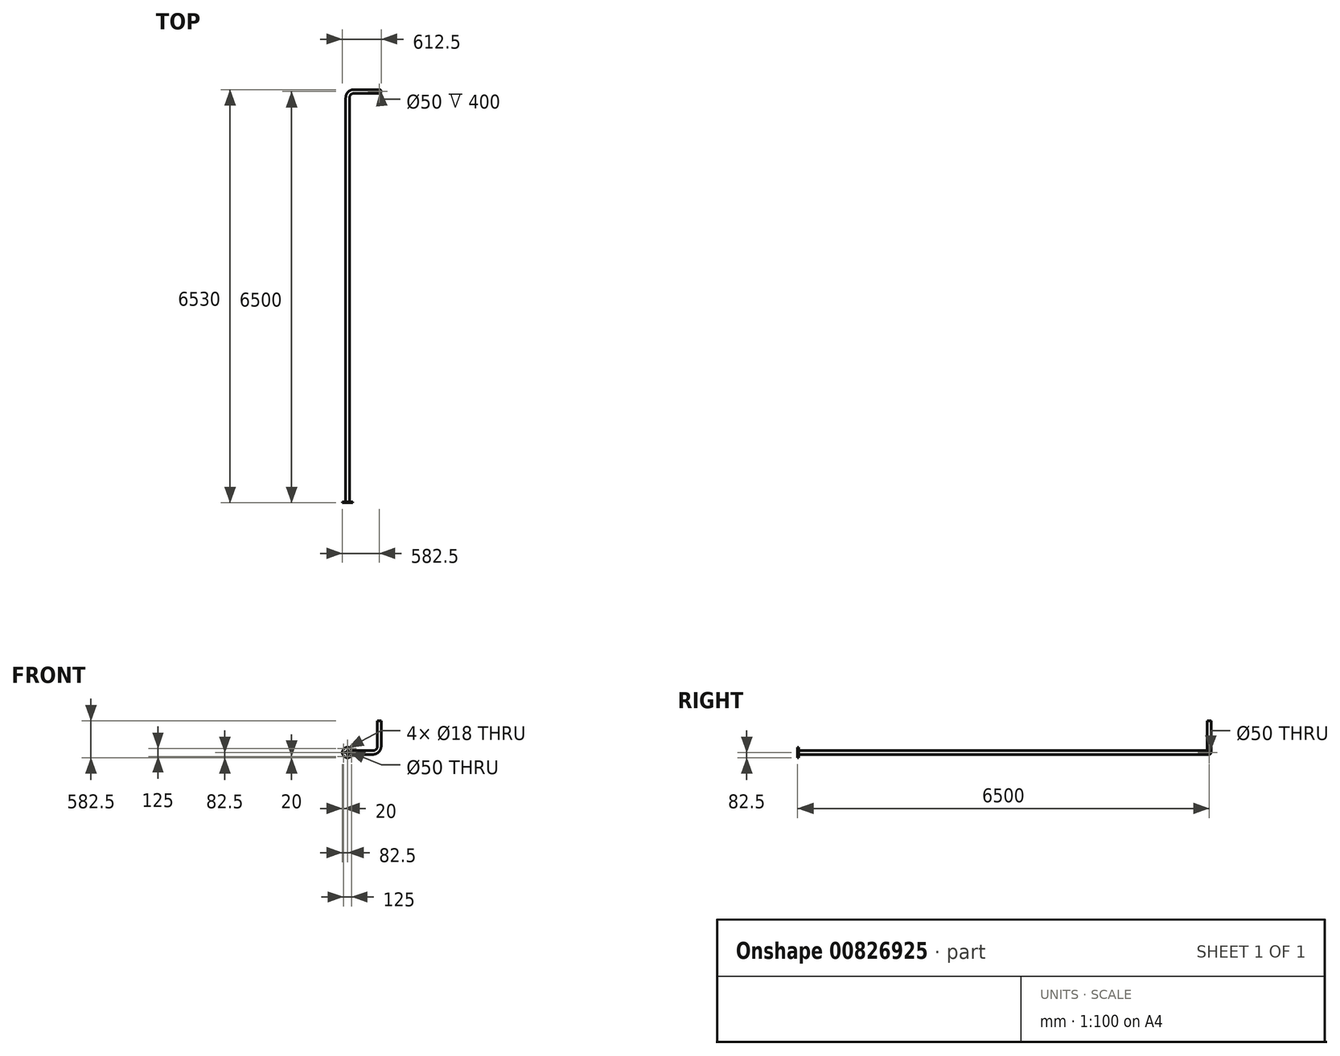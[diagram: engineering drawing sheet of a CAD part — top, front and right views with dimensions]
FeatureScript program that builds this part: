
annotation { "Feature Type Name" : "Feature", "Feature Type Description" : "" }
export const myFeature = defineFeature(function(context is Context, id is Id, definition is map)
    precondition{}
    {
        {
            var Q0;
            Q0=qCreatedBy(makeId("Front.planeOp"),FACE);
            var sketch = newSketch(context, id + "F0", { "sketchPlane" : qUnion([Q0])});
            skCircle(sketch, "E0", {"center": v(0, 0) * mm, "radius": 25 * mm});
            skCircle(sketch, "E1", {"center": v(0, 0) * mm, "radius": 30 * mm});
            skCircle(sketch, "E2", {"center": v(0, 0) * mm, "radius": 82.5 * mm});
            skCircle(sketch, "E3", {"center": v(0, 62.5) * mm, "radius": 9 * mm});
            skCircle(sketch, "E4.1.0", {"center": v(-62.5, 0) * mm, "radius": 9 * mm});
            skCircle(sketch, "E4.2.0", {"center": v(0, -62.5) * mm, "radius": 9 * mm});
            skCircle(sketch, "E4.3.0", {"center": v(62.5, 0) * mm, "radius": 9 * mm});
            skSolve(sketch);
        }
        {
            var Q0;
            Q0=qCreatedBy(makeId("Top.planeOp"),FACE);
            var sketch = newSketch(context, id + "F1", { "sketchPlane" : qUnion([Q0])});
            skLineSegment(sketch, "E5", {"start": v(0, 0) * mm, "end": v(0, 6400) * mm});
            skLineSegment(sketch, "E6", {"start": v(100, 6500) * mm, "end": v(500, 6500) * mm});
            skPoint(sketch, "E7.visualSharp", {"position": v(0, 6500) * mm});
            skArc(sketch, "E7.filletArc", {"start": v(100, 6500) * mm, "mid": v(29.29, 6470.71) * mm, "end": v(0, 6400) * mm});
            skSolve(sketch);
        }
        {
            var Q0;
            Q0=qCreatedBy(makeId("Front.planeOp"),FACE);
            cPlane(context, id + "F2", {"entities" : qUnion([Q0]), "cplaneType" : CPlaneType.OFFSET, "offset" : 6500 * mm, "oppositeDirection" : true, "width" : 150 * mm, "height" : 150 * mm});
        }
        {
            var Q0;
            Q0=qCreatedBy(id+"F2.planeOp",FACE);
            var sketch = newSketch(context, id + "F3", { "sketchPlane" : qUnion([Q0])});
            skLineSegment(sketch, "E8.0", {"start": v(100, 0) * mm, "end": v(400, 0) * mm});
            skLineSegment(sketch, "E9", {"start": v(500, 100) * mm, "end": v(500, 500) * mm});
            skPoint(sketch, "E10.visualSharp", {"position": v(500, 0) * mm});
            skArc(sketch, "E10.filletArc", {"start": v(400, 0) * mm, "mid": v(470.71, 29.29) * mm, "end": v(500, 100) * mm});
            skSolve(sketch);
        }
        {
            var Q0;
            Q0=makeQuery(id+"F0.imprint","IMPRINT",FACE,{"disambiguationData":[TD([[makeQuery(id+"F0.imprint","IMPRINT",EDGE,{"derivedFrom":sQuery(id+"F0.wireOp",EDGE,"E0")}),-1.0]])]});
            var Q1;
            Q1=sQuery(id+"F1.wireOp",EDGE,"E5");
            var Q2;
            Q2=sQuery(id+"F1.wireOp",EDGE,"E7.filletArc");
            var Q3;
            Q3=sQuery(id+"F3.wireOp",EDGE,"E8.0");
            var Q4;
            Q4=sQuery(id+"F3.wireOp",EDGE,"E10.filletArc");
            var Q5;
            Q5=sQuery(id+"F3.wireOp",EDGE,"E9");
            sweep(context, id + "F4", {"profiles" : qUnion([Q0]), "path" : qUnion([Q1, Q2, Q3, Q4, Q5])});
        }
        {
            var Q0;
            Q0=makeQuery(id+"F0.imprint","IMPRINT",FACE,{"disambiguationData":[TD([[makeQuery(id+"F0.imprint","IMPRINT",EDGE,{"derivedFrom":sQuery(id+"F0.wireOp",EDGE,"E1")}),-1.0]])]});
            extrude(context, id + "F5", {"entities" : qUnion([Q0]), "operationType" : NewBodyOperationType.ADD, "oppositeDirection" : true, "depth" : 15 * mm, "offsetDistance" : 25 * mm});
        }
    });
